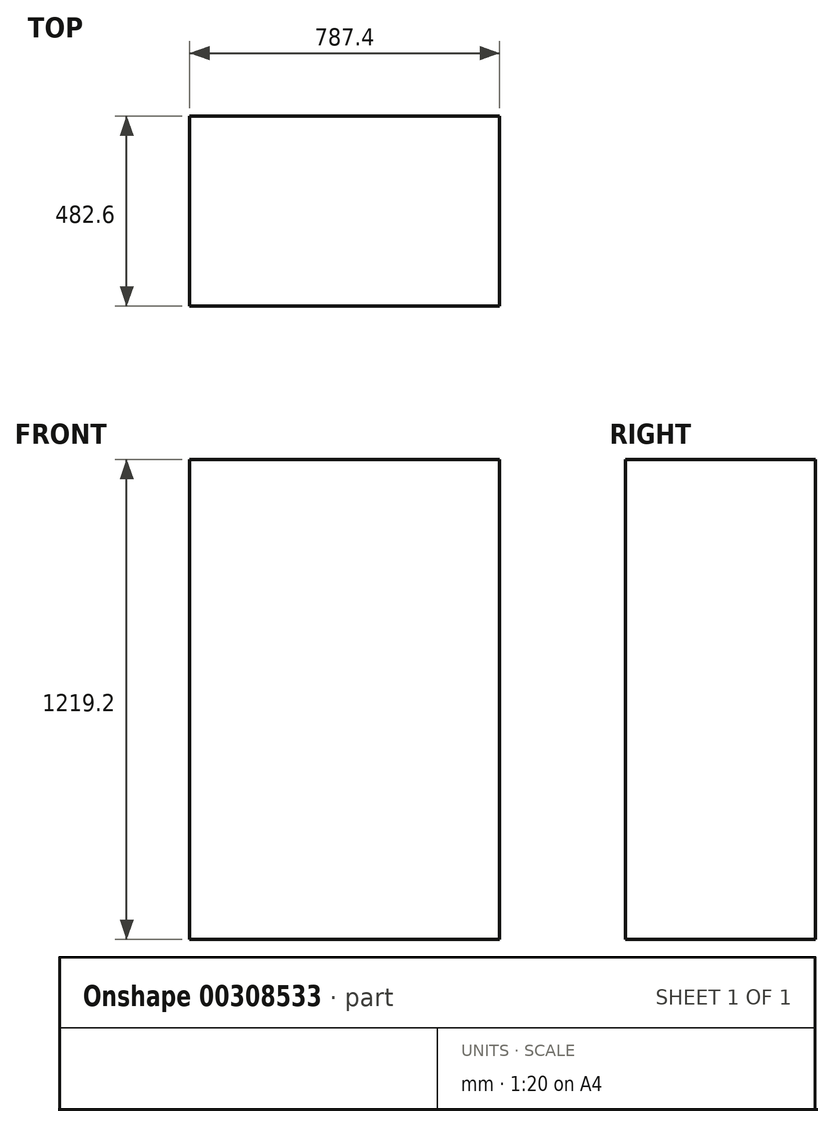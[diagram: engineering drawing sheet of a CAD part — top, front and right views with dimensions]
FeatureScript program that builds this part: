
annotation { "Feature Type Name" : "Feature", "Feature Type Description" : "" }
export const myFeature = defineFeature(function(context is Context, id is Id, definition is map)
    precondition{}
    {
        {
            var Q0;
            Q0=qCreatedBy(makeId("Top.planeOp"),FACE);
            var sketch = newSketch(context, id + "F0", { "sketchPlane" : qUnion([Q0])});
            skLineSegment(sketch, "E0.bottom", {"start": v(393.7, -241.3) * mm, "end": v(-393.7, -241.3) * mm});
            skLineSegment(sketch, "E0.top", {"start": v(393.7, 241.3) * mm, "end": v(-393.7, 241.3) * mm});
            skLineSegment(sketch, "E0.left", {"start": v(393.7, -241.3) * mm, "end": v(393.7, 241.3) * mm});
            skLineSegment(sketch, "E0.right", {"start": v(-393.7, -241.3) * mm, "end": v(-393.7, 241.3) * mm});
            skPoint(sketch, "E0.middle", {"position": v(0, 0) * mm});
            skSolve(sketch);
        }
        {
            var Q0;
            Q0=makeQuery(id+"F0.imprint","IMPRINT",FACE,{"disambiguationData":[TD([[makeQuery(id+"F0.imprint","IMPRINT",EDGE,{"derivedFrom":sQuery(id+"F0.wireOp",EDGE,"E0.bottom")}),-1.0]])]});
            extrude(context, id + "F1", {"entities" : qUnion([Q0]), "depth" : 1219.2 * mm});
        }
    });
